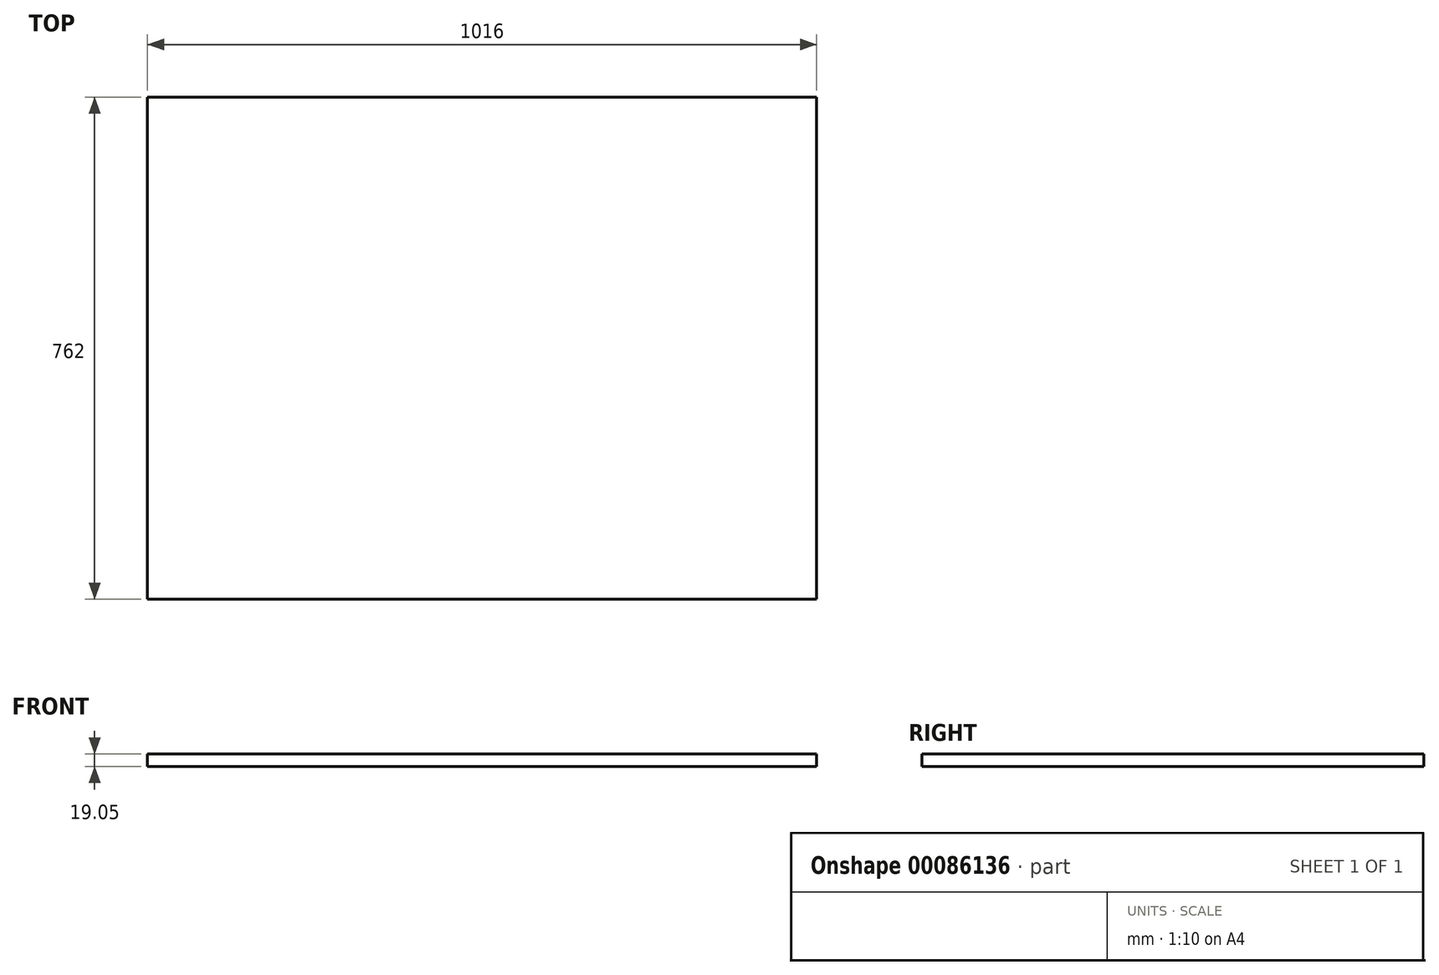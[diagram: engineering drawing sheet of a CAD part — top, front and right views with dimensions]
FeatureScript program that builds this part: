
annotation { "Feature Type Name" : "Feature", "Feature Type Description" : "" }
export const myFeature = defineFeature(function(context is Context, id is Id, definition is map)
    precondition{}
    {
        {
            var Q0;
            Q0=qCreatedBy(makeId("Top.planeOp"),FACE);
            var sketch = newSketch(context, id + "F0", { "sketchPlane" : qUnion([Q0])});
            skLineSegment(sketch, "E0.bottom", {"start": v(508, -381) * mm, "end": v(-508, -381) * mm});
            skLineSegment(sketch, "E0.top", {"start": v(508, 381) * mm, "end": v(-508, 381) * mm});
            skLineSegment(sketch, "E0.left", {"start": v(508, -381) * mm, "end": v(508, 381) * mm});
            skLineSegment(sketch, "E0.right", {"start": v(-508, -381) * mm, "end": v(-508, 381) * mm});
            skPoint(sketch, "E0.middle", {"position": v(0, 0) * mm});
            skSolve(sketch);
        }
        {
            var Q0;
            Q0 = qSketchRegion(id + "F0", true);
            extrude(context, id + "F1", {"entities" : qUnion([Q0]), "depth" : 19.05 * mm});
        }
    });
